# Revit family: Lighting_Fixture-Wall-Astro-Palermo
name_source: partatom
category: Lighting Fixtures
revit_build: Autodesk Revit 2014 (Build: 20130308_1515(x64)
units: mm (PartAtom-declared; Revit-internal decimal feet)

## types (5) — shared parameters
Assembly Code = D5020200
Casing Material = Astro - Aluminium - Chrome Finish
Class = 2
Color Filter = 16777215
Description = Mirror Light
Dimmable = No
Dimming Lamp Color Temperature Shift = <None>
Emit Shape Visible in Rendering = No
Emit from Rectangle Length = 36 mm  [stored 0.11811 ft]
Height = 40 mm  [stored 0.131234 ft]
IP Rating = IP44
Lamp = T5
Lamp included = No
Length = 61 mm  [stored 0.200131 ft]
Light Source Elevation = 1600 mm  [stored 5.24934 ft]
Light Source From Wall = 45.5 mm  [stored 0.149278 ft]
Manufacturer = Astro Lighting Ltd, CM20 2DP
Mountable on normally flammable surfaces = Yes
Number of Poles = 1
Suitable for bathroom zone = Zone 2, 3
Tilt Angle = 90.00°
Type Comments = - Can be mounted horizontally or vertically
 - Includes integral electronic ballast
URL = www.astrolighting.co.uk
Voltage = 230 V

## per-type parameters (varying)
| type | Apparent Load | Cable Entry Placer (from right) | Diffuser Length | Emit from Rectangle Width | Energy Efficiency Rating | Luminaire Lamp Efficiency Rating | Photometric Web File | Product Documentation | Wattage Comments | Weight | Width |
| 0780 Palermo 600 | 15 VA | 211 mm  [stored 0.692257 ft] | 402 mm  [stored 1.3189 ft] | 402 mm  [stored 1.3189 ft] | A | A*-C | 0780 palermo 600.ies | http://www.astrolighting.co.uk
products/kw/0780/0780_Palermo-600 | 28W | 1.9 kg | 602 mm  [stored 1.97507 ft] |
| 0837 Palermo 600 HO | 37 VA | 211 mm  [stored 0.692257 ft] | 402 mm  [stored 1.3189 ft] | 402 mm  [stored 1.3189 ft] |  | A*-A | 0837 palermo 600 high output.ies | http://www.astrolighting.co.uk
products/kw/0837/0837
_Palermo-600-(Hi-Output) | 24W | 1.07 kg | 602 mm  [stored 1.97507 ft] |
| 0479 Palermo 900 | 23 VA | 450 mm  [stored 1.47638 ft] | 700 mm  [stored 2.29659 ft] | 700 mm  [stored 2.29659 ft] | - | A*-A | 0479 PALERMO 900.ies | http://www.astrolighting.co.uk
/kw/0479/0479_Palermo-900 | 21W | 1.47 kg | 900 mm  [stored 2.95276 ft] |
| 0838 Palermo 900 HO | 37 VA | 450 mm  [stored 1.47638 ft] | 700 mm  [stored 2.29659 ft] | 700 mm  [stored 2.29659 ft] | - | A*-A | 0838 PALERMO 900 HIGH OUTPUT.ies | http://www.astrolighting.co.uk
/kw/0838/0838_Palermo-900-(Hi-Output) | 39W | 1.5 kg | 900 mm  [stored 2.95276 ft] |
| 0627 Palermo 1200 | 30 VA | 601 mm  [stored 1.97178 ft] | 1002 mm  [stored 3.2874 ft] | 1002 mm  [stored 3.2874 ft] | A | A*-C | 0627 PALERMO 1200.ies | http://www.astrolighting.co.uk
products/kw/0627/0627_Palermo-1200 | 28W | 1.9 kg | 1202 mm  [stored 3.94357 ft] |

note: column(s) folded — value = type name in every type: Model

note: [stored X ft] marks values corroborated as IEEE doubles in the binary element streams (Revit-internal decimal feet)
